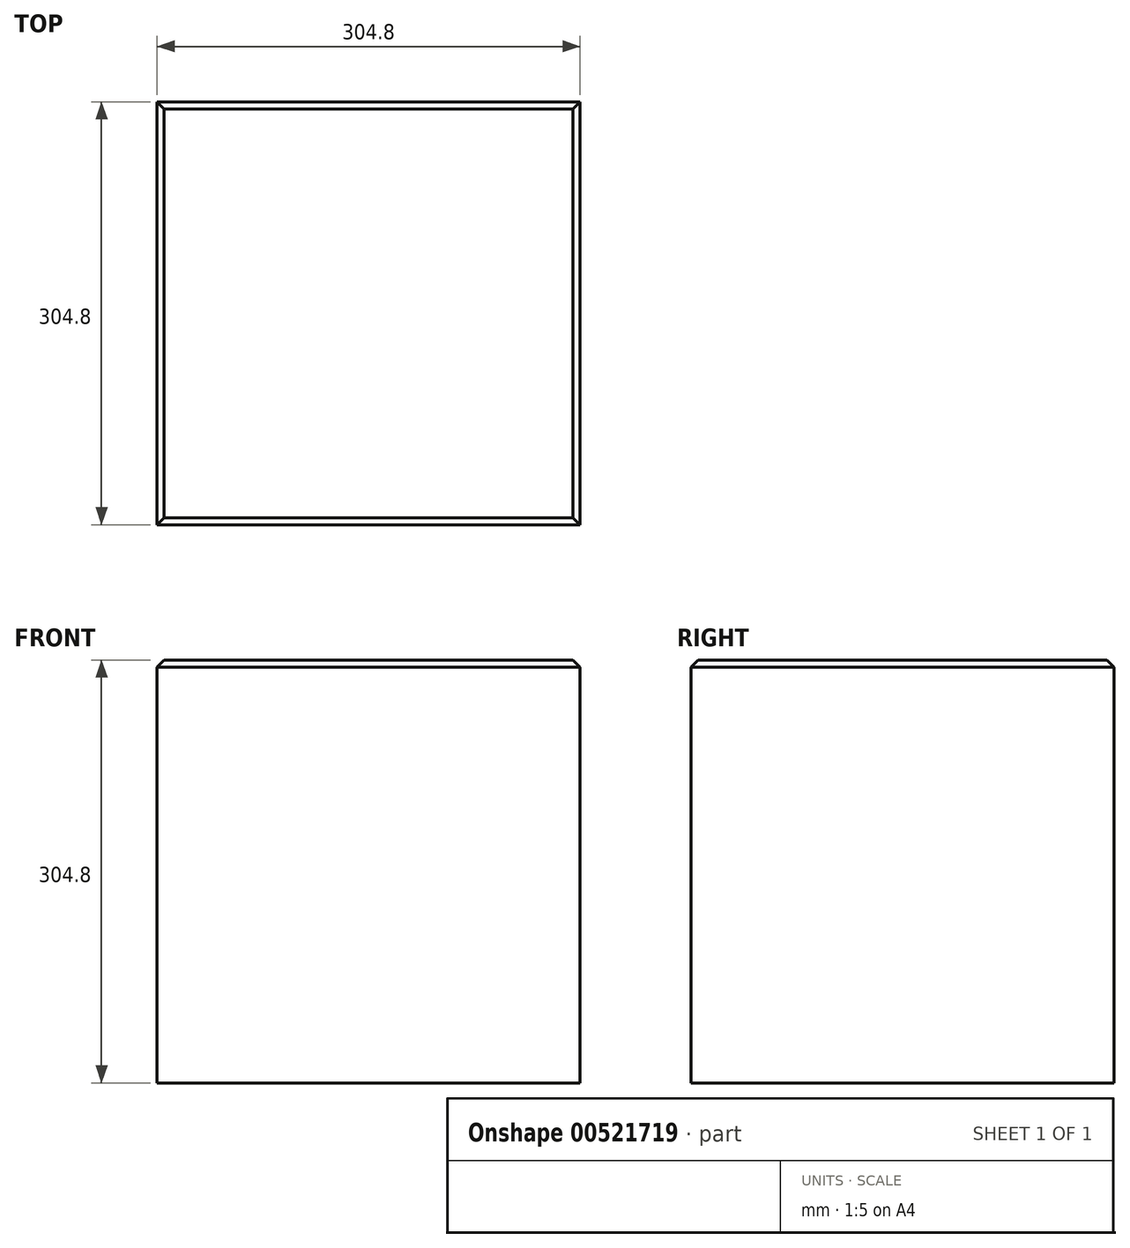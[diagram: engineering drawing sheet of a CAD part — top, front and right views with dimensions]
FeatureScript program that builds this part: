
annotation { "Feature Type Name" : "Feature", "Feature Type Description" : "" }
export const myFeature = defineFeature(function(context is Context, id is Id, definition is map)
    precondition{}
    {
        {
            var Q0;
            Q0=qCreatedBy(makeId("Top.planeOp"),FACE);
            var sketch = newSketch(context, id + "F0", { "sketchPlane" : qUnion([Q0])});
            skLineSegment(sketch, "E0.bottom", {"start": v(116.79, 168.09) * mm, "end": v(-188.01, 168.09) * mm});
            skLineSegment(sketch, "E0.top", {"start": v(116.79, -136.71) * mm, "end": v(-188.01, -136.71) * mm});
            skLineSegment(sketch, "E0.left", {"start": v(116.79, 168.09) * mm, "end": v(116.79, -136.71) * mm});
            skLineSegment(sketch, "E0.right", {"start": v(-188.01, 168.09) * mm, "end": v(-188.01, -136.71) * mm});
            skPoint(sketch, "E0.middle", {"position": v(-35.61, 15.69) * mm});
            skSolve(sketch);
        }
        {
            var Q0;
            Q0 = qSketchRegion(id + "F0", true);
            extrude(context, id + "F1", {"entities" : qUnion([Q0]), "depth" : 304.8 * mm, "offsetDistance" : 25.4 * mm});
        }
        {
            var Q0;
            Q0=makeQuery(id+"F1.opExtrude","CAP_EDGE",EDGE,{"disambiguationData":[OSD([sQuery(id+"F0.wireOp",EDGE,"E0.top")])],"isStart":false});
            var Q1;
            Q1=makeQuery(id+"F1.opExtrude","CAP_EDGE",EDGE,{"disambiguationData":[OSD([sQuery(id+"F0.wireOp",EDGE,"E0.left")])],"isStart":false});
            var Q2;
            Q2=makeQuery(id+"F1.opExtrude","CAP_EDGE",EDGE,{"disambiguationData":[OSD([sQuery(id+"F0.wireOp",EDGE,"E0.right")])],"isStart":false});
            var Q3;
            Q3=makeQuery(id+"F1.opExtrude","CAP_EDGE",EDGE,{"disambiguationData":[OSD([sQuery(id+"F0.wireOp",EDGE,"E0.bottom")])],"isStart":false});
            chamfer(context, id + "F2", {"entities" : qUnion([Q0, Q1, Q2, Q3]), "width" : 5.08 * mm, "tangentPropagation" : true});
        }
    });
